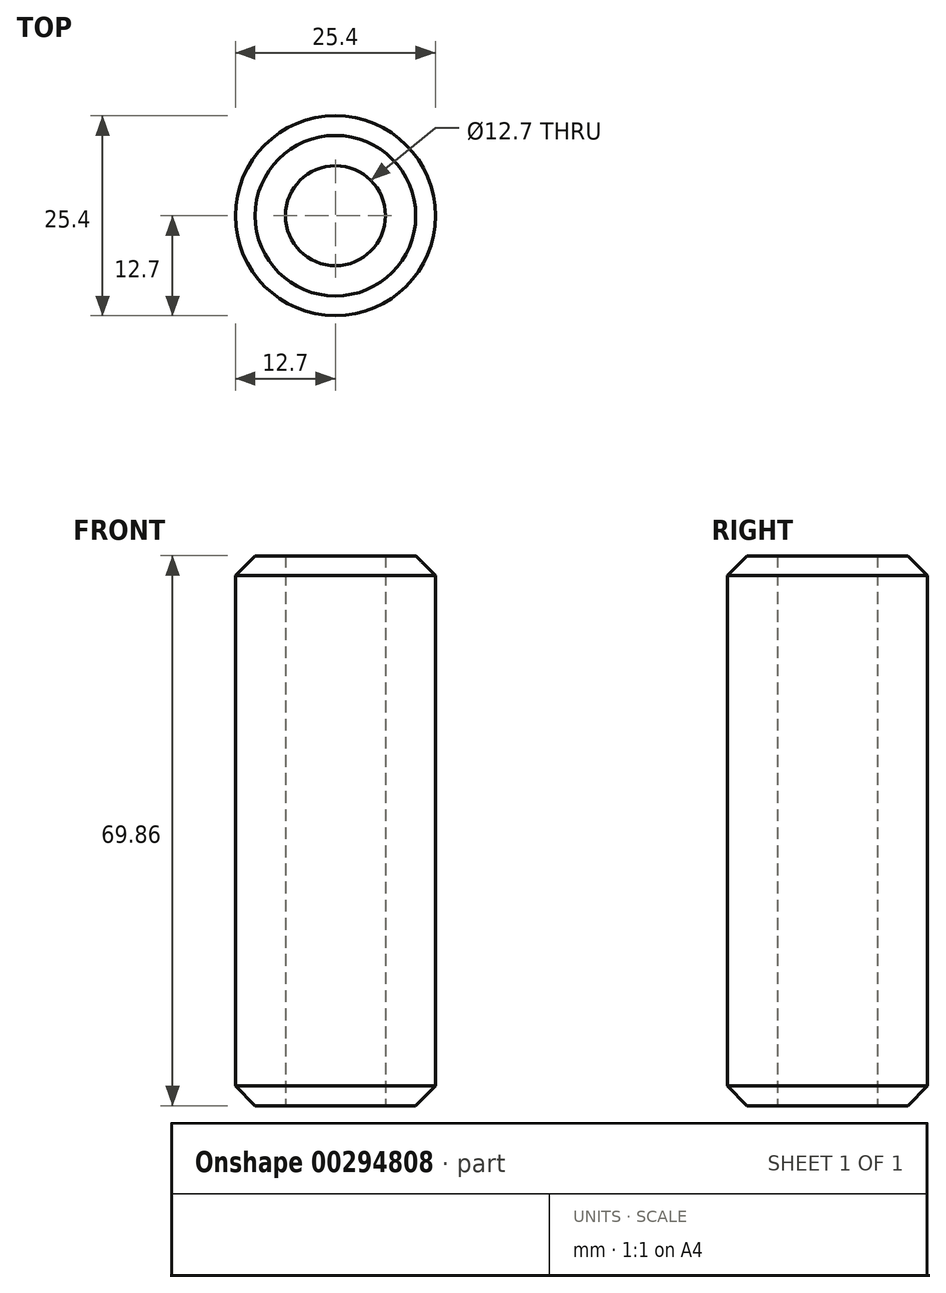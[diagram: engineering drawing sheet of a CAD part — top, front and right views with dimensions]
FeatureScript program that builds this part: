
annotation { "Feature Type Name" : "Feature", "Feature Type Description" : "" }
export const myFeature = defineFeature(function(context is Context, id is Id, definition is map)
    precondition{}
    {
        {
            var Q0;
            Q0=qCreatedBy(makeId("Top.planeOp"),FACE);
            var sketch = newSketch(context, id + "F0", { "sketchPlane" : qUnion([Q0])});
            skCircle(sketch, "E0", {"center": v(0, 0) * mm, "radius": 12.7 * mm});
            skCircle(sketch, "E1", {"center": v(0, 0) * mm, "radius": 6.35 * mm});
            skSolve(sketch);
        }
        {
            var Q0;
            Q0=makeQuery(id+"F0.imprint","IMPRINT",FACE,{"disambiguationData":[TD([[makeQuery(id+"F0.imprint","IMPRINT",EDGE,{"derivedFrom":sQuery(id+"F0.wireOp",EDGE,"E0")}),1.0]])]});
            extrude(context, id + "F1", {"entities" : qUnion([Q0]), "endBound" : BoundingType.SYMMETRIC, "depth" : 69.85 * mm});
        }
        {
            var Q0;
            Q0=makeQuery(id+"F1.opExtrude","CAP_EDGE",EDGE,{"disambiguationData":[OSD([sQuery(id+"F0.wireOp",EDGE,"E0")])],"isStart":false});
            var Q1;
            Q1=makeQuery(id+"F1.opExtrude","CAP_EDGE",EDGE,{"disambiguationData":[OSD([sQuery(id+"F0.wireOp",EDGE,"E0")])],"isStart":true});
            chamfer(context, id + "F2", {"entities" : qUnion([Q0, Q1]), "width" : 2.5 * mm, "tangentPropagation" : true});
        }
    });
